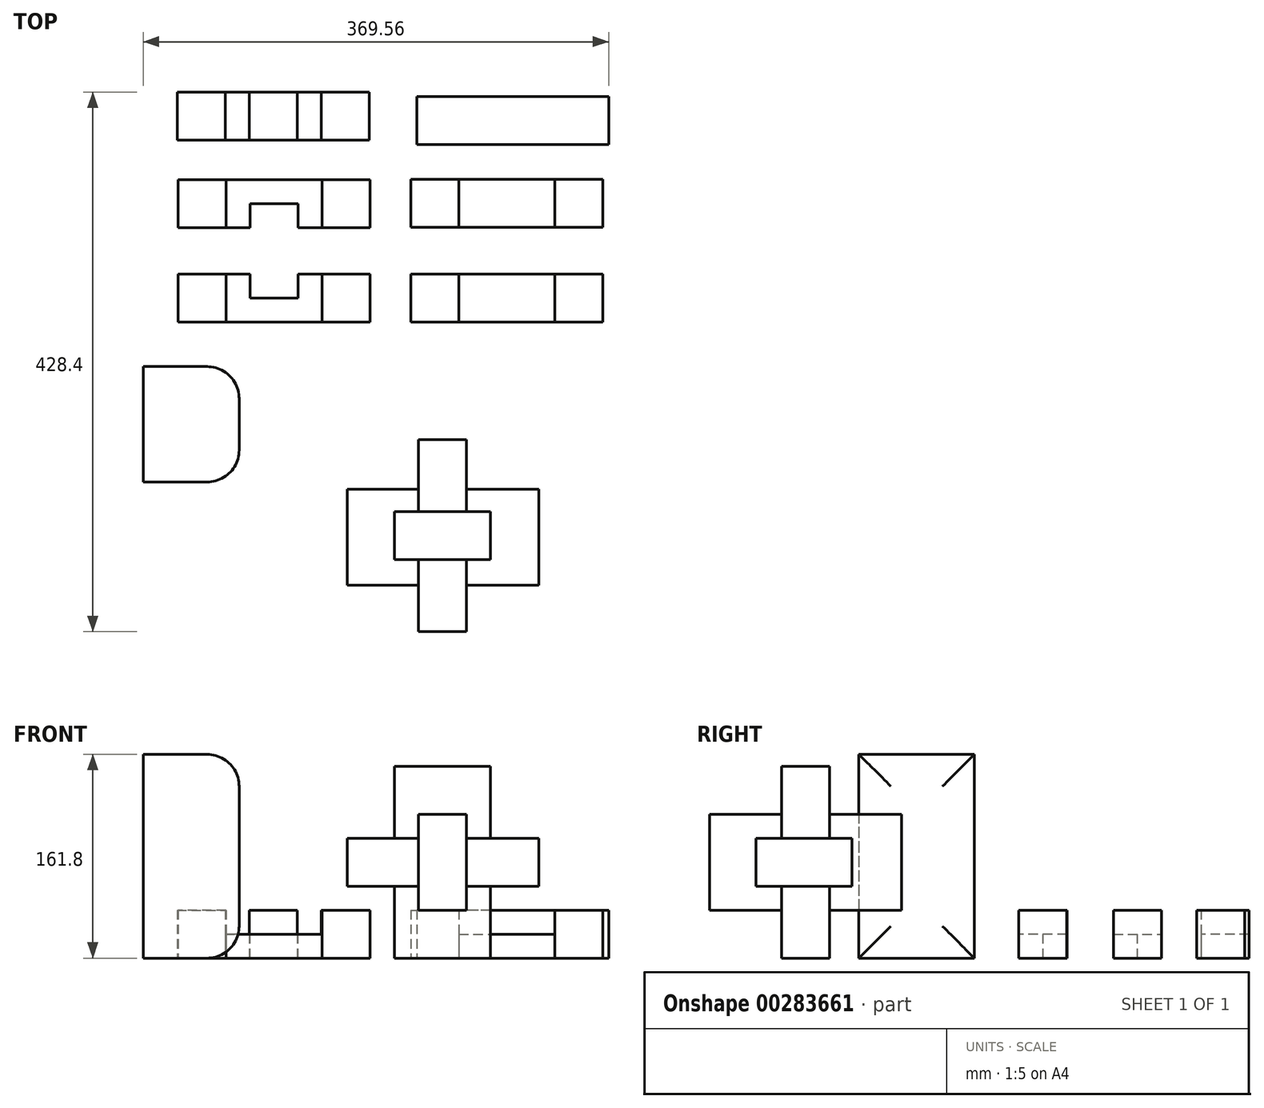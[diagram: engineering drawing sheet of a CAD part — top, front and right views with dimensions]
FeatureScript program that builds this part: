
annotation { "Feature Type Name" : "Feature", "Feature Type Description" : "" }
export const myFeature = defineFeature(function(context is Context, id is Id, definition is map)
    precondition{}
    {
        {
            var Q0;
            Q0=qCreatedBy(makeId("Top.planeOp"),FACE);
            var sketch = newSketch(context, id + "F0", { "sketchPlane" : qUnion([Q0])});
            skLineSegment(sketch, "E0", {"start": v(-72.38, -56.7) * mm, "end": v(80.02, -56.7) * mm});
            skLineSegment(sketch, "E1.top", {"start": v(-72.38, -18.6) * mm, "end": v(80.02, -18.6) * mm});
            skLineSegment(sketch, "E1.left", {"start": v(-72.38, -56.7) * mm, "end": v(-72.38, -18.6) * mm});
            skLineSegment(sketch, "E1.right", {"start": v(80.02, -56.7) * mm, "end": v(80.02, -18.6) * mm});
            skLineSegment(sketch, "E2", {"start": v(-72.38, -18.6) * mm, "end": v(-34.28, -18.6) * mm, "construction": true});
            skLineSegment(sketch, "E3", {"start": v(-34.28, -18.6) * mm, "end": v(3.82, -18.6) * mm, "construction": true});
            skLineSegment(sketch, "E4", {"start": v(3.82, -18.6) * mm, "end": v(41.92, -18.6) * mm, "construction": true});
            skLineSegment(sketch, "E5", {"start": v(41.92, -18.6) * mm, "end": v(80.02, -18.6) * mm, "construction": true});
            skLineSegment(sketch, "E6", {"start": v(-34.28, -18.6) * mm, "end": v(-34.28, -56.7) * mm});
            skLineSegment(sketch, "E7", {"start": v(41.92, -18.6) * mm, "end": v(41.92, -56.7) * mm});
            skSolve(sketch);
        }
        {
            var Q0;
            {var subQ0=sQuery(id+"F0.wireOp",EDGE,"E1.left");Q0=makeQuery(id+"F0.imprint","IMPRINT",FACE,{"disambiguationData":[TD([[makeQuery(id+"F0.imprint","IMPRINT",EDGE,{"derivedFrom":subQ0}),-1.0]])]});}
            var Q1;
            {var subQ0=sQuery(id+"F0.wireOp",EDGE,"E1.right");Q1=makeQuery(id+"F0.imprint","IMPRINT",FACE,{"disambiguationData":[TD([[makeQuery(id+"F0.imprint","IMPRINT",EDGE,{"derivedFrom":subQ0}),1.0]])]});}
            extrude(context, id + "F1", {"entities" : qUnion([Q0, Q1]), "depth" : 38.1 * mm});
        }
        {
            var Q0;
            {var subQ0=sQuery(id+"F0.wireOp",EDGE,"E6");Q0=makeQuery(id+"F0.imprint","IMPRINT",FACE,{"disambiguationData":[TD([[makeQuery(id+"F0.imprint","IMPRINT",EDGE,{"derivedFrom":subQ0}),1.0]])]});}
            extrude(context, id + "F2", {"entities" : qUnion([Q0]), "depth" : 19.05 * mm});
        }
        {
            var Q0;
            Q0=makeQuery(id+"F1.opExtrude","SWEPT_BODY",BODY,{"disambiguationData":[OSD([sQuery(id+"F0.wireOp",EDGE,"E0"),sQuery(id+"F0.wireOp",EDGE,"E1.top"),sQuery(id+"F0.wireOp",EDGE,"E1.left"),sQuery(id+"F0.wireOp",EDGE,"E6")])]});
            var Q1;
            Q1=makeQuery(id+"F2.opExtrude","SWEPT_BODY",BODY,{"disambiguationData":[OSD([sQuery(id+"F0.wireOp",EDGE,"E0"),sQuery(id+"F0.wireOp",EDGE,"E1.top"),sQuery(id+"F0.wireOp",EDGE,"E6"),sQuery(id+"F0.wireOp",EDGE,"E7")])]});
            var Q2;
            Q2=makeQuery(id+"F1.opExtrude","SWEPT_BODY",BODY,{"disambiguationData":[OSD([sQuery(id+"F0.wireOp",EDGE,"E0"),sQuery(id+"F0.wireOp",EDGE,"E1.top"),sQuery(id+"F0.wireOp",EDGE,"E1.right"),sQuery(id+"F0.wireOp",EDGE,"E7")])]});
            var Q3;
            Q3=qCreatedBy(makeId("Front.planeOp"),FACE);
            mirror(context, id + "F3", {"entities" : qUnion([Q0, Q1, Q2]), "mirrorPlane" : qUnion([Q3])});
        }
        {
            var Q0;
            Q0=qCreatedBy(makeId("Top.planeOp"),FACE);
            var sketch = newSketch(context, id + "F4", { "sketchPlane" : qUnion([Q0])});
            skLineSegment(sketch, "E8.bottom", {"start": v(-104.95, -56.55) * mm, "end": v(-257.35, -56.55) * mm});
            skLineSegment(sketch, "E8.top", {"start": v(-104.95, -18.45) * mm, "end": v(-257.35, -18.45) * mm});
            skLineSegment(sketch, "E8.left", {"start": v(-104.95, -56.55) * mm, "end": v(-104.95, -18.45) * mm});
            skLineSegment(sketch, "E8.right", {"start": v(-257.35, -56.55) * mm, "end": v(-257.35, -18.45) * mm});
            skLineSegment(sketch, "E9", {"start": v(-104.95, -18.45) * mm, "end": v(-143.05, -18.45) * mm, "construction": true});
            skLineSegment(sketch, "E10", {"start": v(-143.05, -18.45) * mm, "end": v(-257.35, -18.45) * mm, "construction": true});
            skLineSegment(sketch, "E11", {"start": v(-219.25, -18.45) * mm, "end": v(-257.35, -18.45) * mm, "construction": true});
            skLineSegment(sketch, "E12", {"start": v(-143.05, -18.45) * mm, "end": v(-143.05, -56.55) * mm});
            skLineSegment(sketch, "E13", {"start": v(-219.25, -18.45) * mm, "end": v(-219.25, -56.55) * mm});
            skSolve(sketch);
        }
        {
            var Q0;
            {var subQ0=sQuery(id+"F4.wireOp",EDGE,"E8.left");Q0=makeQuery(id+"F4.imprint","IMPRINT",FACE,{"disambiguationData":[TD([[makeQuery(id+"F4.imprint","IMPRINT",EDGE,{"derivedFrom":subQ0}),1.0]])]});}
            var Q1;
            {var subQ0=sQuery(id+"F4.wireOp",EDGE,"E8.right");Q1=makeQuery(id+"F4.imprint","IMPRINT",FACE,{"disambiguationData":[TD([[makeQuery(id+"F4.imprint","IMPRINT",EDGE,{"derivedFrom":subQ0}),-1.0]])]});}
            extrude(context, id + "F5", {"entities" : qUnion([Q0, Q1]), "operationType" : NewBodyOperationType.ADD, "depth" : 38.1 * mm});
        }
        {
            var Q0;
            {var subQ0=sQuery(id+"F4.wireOp",EDGE,"E12");Q0=makeQuery(id+"F4.imprint","IMPRINT",FACE,{"disambiguationData":[TD([[makeQuery(id+"F4.imprint","IMPRINT",EDGE,{"derivedFrom":subQ0}),-1.0]])]});}
            extrude(context, id + "F6", {"entities" : qUnion([Q0]), "depth" : 19.05 * mm});
        }
        {
            var Q0;
            Q0=makeQuery(id+"F6.opExtrude","CAP_FACE",FACE,{"disambiguationData":[OSD([sQuery(id+"F4.wireOp",EDGE,"E8.bottom"),sQuery(id+"F4.wireOp",EDGE,"E8.top"),sQuery(id+"F4.wireOp",EDGE,"E12"),sQuery(id+"F4.wireOp",EDGE,"E13")])],"isStart":false});
            var sketch = newSketch(context, id + "F7", { "sketchPlane" : qUnion([Q0])});
            skLineSegment(sketch, "E14", {"start": v(-219.25, -18.45) * mm, "end": v(-200.2, -18.45) * mm, "construction": true});
            skLineSegment(sketch, "E15", {"start": v(-200.2, -18.45) * mm, "end": v(-200.2, -37.5) * mm, "construction": true});
            skLineSegment(sketch, "E16", {"start": v(-200.2, -18.45) * mm, "end": v(-200.2, -37.5) * mm});
            skLineSegment(sketch, "E17", {"start": v(-162.1, -37.5) * mm, "end": v(-200.2, -37.5) * mm});
            skLineSegment(sketch, "E18", {"start": v(-162.1, -37.5) * mm, "end": v(-162.1, -18.45) * mm});
            skSolve(sketch);
        }
        {
            var Q0;
            {var subQ0=sQuery(id+"F7.wireOp",EDGE,"E16");Q0=makeQuery(id+"F7.imprint","IMPRINT",FACE,{"disambiguationData":[TD([[makeQuery(id+"F7.imprint","IMPRINT",EDGE,{"derivedFrom":subQ0}),1.0]])]});}
            extrude(context, id + "F8", {"entities" : qUnion([Q0]), "operationType" : NewBodyOperationType.REMOVE, "oppositeDirection" : true, "depth" : 19.05 * mm});
        }
        {
            var Q0;
            Q0=makeQuery(id+"F5.opExtrude","SWEPT_BODY",BODY,{"disambiguationData":[OSD([sQuery(id+"F4.wireOp",EDGE,"E8.bottom"),sQuery(id+"F4.wireOp",EDGE,"E8.top"),sQuery(id+"F4.wireOp",EDGE,"E8.left"),sQuery(id+"F4.wireOp",EDGE,"E12")])]});
            var Q1;
            Q1=makeQuery(id+"F6.opExtrude","SWEPT_BODY",BODY,{"disambiguationData":[OSD([sQuery(id+"F4.wireOp",EDGE,"E8.bottom"),sQuery(id+"F4.wireOp",EDGE,"E8.top"),sQuery(id+"F4.wireOp",EDGE,"E12"),sQuery(id+"F4.wireOp",EDGE,"E13")])]});
            var Q2;
            Q2=makeQuery(id+"F5.opExtrude","SWEPT_BODY",BODY,{"disambiguationData":[OSD([sQuery(id+"F4.wireOp",EDGE,"E8.bottom"),sQuery(id+"F4.wireOp",EDGE,"E8.top"),sQuery(id+"F4.wireOp",EDGE,"E8.right"),sQuery(id+"F4.wireOp",EDGE,"E13")])]});
            var Q3;
            Q3=qCreatedBy(makeId("Front.planeOp"),FACE);
            mirror(context, id + "F9", {"entities" : qUnion([Q0, Q1, Q2]), "mirrorPlane" : qUnion([Q3])});
        }
        {
            var Q0;
            Q0=qCreatedBy(makeId("Top.planeOp"),FACE);
            var sketch = newSketch(context, id + "F10", { "sketchPlane" : qUnion([Q0])});
            skLineSegment(sketch, "E19.bottom", {"start": v(84.58, 84.4) * mm, "end": v(-67.82, 84.4) * mm});
            skLineSegment(sketch, "E19.top", {"start": v(84.58, 122.5) * mm, "end": v(-67.82, 122.5) * mm});
            skLineSegment(sketch, "E19.left", {"start": v(84.58, 84.4) * mm, "end": v(84.58, 122.5) * mm});
            skLineSegment(sketch, "E19.right", {"start": v(-67.82, 84.4) * mm, "end": v(-67.82, 122.5) * mm});
            skSolve(sketch);
        }
        {
            var Q0;
            Q0=makeQuery(id+"F10.imprint","IMPRINT",FACE,{"disambiguationData":[TD([[makeQuery(id+"F10.imprint","IMPRINT",EDGE,{"derivedFrom":sQuery(id+"F10.wireOp",EDGE,"E19.bottom")}),-1.0]])]});
            extrude(context, id + "F11", {"entities" : qUnion([Q0]), "depth" : 38.1 * mm});
        }
        {
            var Q0;
            Q0=qCreatedBy(makeId("Top.planeOp"),FACE);
            var sketch = newSketch(context, id + "F12", { "sketchPlane" : qUnion([Q0])});
            skLineSegment(sketch, "E20.bottom", {"start": v(-257.97, 87.96) * mm, "end": v(-105.57, 87.96) * mm});
            skLineSegment(sketch, "E20.top", {"start": v(-257.97, 126.06) * mm, "end": v(-105.57, 126.06) * mm});
            skLineSegment(sketch, "E20.left", {"start": v(-257.97, 87.96) * mm, "end": v(-257.97, 126.06) * mm});
            skLineSegment(sketch, "E20.right", {"start": v(-105.57, 87.96) * mm, "end": v(-105.57, 126.06) * mm});
            skLineSegment(sketch, "E21.bottom", {"start": v(-257.97, 126.06) * mm, "end": v(-219.87, 126.06) * mm, "construction": true});
            skLineSegment(sketch, "E21.top", {"start": v(-257.97, 126.06) * mm, "end": v(-219.87, 126.06) * mm, "construction": true});
            skLineSegment(sketch, "E21.left", {"start": v(-257.97, 126.06) * mm, "end": v(-257.97, 126.06) * mm});
            skLineSegment(sketch, "E21.right", {"start": v(-219.87, 126.06) * mm, "end": v(-219.87, 126.06) * mm});
            skLineSegment(sketch, "E22.bottom", {"start": v(-105.57, 126.06) * mm, "end": v(-143.67, 126.06) * mm, "construction": true});
            skLineSegment(sketch, "E22.top", {"start": v(-105.57, 126.06) * mm, "end": v(-143.67, 126.06) * mm, "construction": true});
            skLineSegment(sketch, "E22.left", {"start": v(-105.57, 126.06) * mm, "end": v(-105.57, 126.06) * mm});
            skLineSegment(sketch, "E22.right", {"start": v(-143.67, 126.06) * mm, "end": v(-143.67, 126.06) * mm});
            skLineSegment(sketch, "E23.bottom", {"start": v(-219.87, 126.06) * mm, "end": v(-200.82, 126.06) * mm, "construction": true});
            skLineSegment(sketch, "E23.top", {"start": v(-219.87, 126.06) * mm, "end": v(-200.82, 126.06) * mm, "construction": true});
            skLineSegment(sketch, "E23.right", {"start": v(-200.82, 126.06) * mm, "end": v(-200.82, 126.06) * mm});
            skLineSegment(sketch, "E24.bottom", {"start": v(-143.67, 126.06) * mm, "end": v(-162.72, 126.06) * mm, "construction": true});
            skLineSegment(sketch, "E24.top", {"start": v(-143.67, 126.06) * mm, "end": v(-162.72, 126.06) * mm, "construction": true});
            skLineSegment(sketch, "E24.right", {"start": v(-162.72, 126.06) * mm, "end": v(-162.72, 126.06) * mm});
            skLineSegment(sketch, "E25", {"start": v(-219.87, 126.06) * mm, "end": v(-219.87, 87.96) * mm});
            skLineSegment(sketch, "E26", {"start": v(-200.82, 126.06) * mm, "end": v(-200.82, 87.96) * mm});
            skLineSegment(sketch, "E27", {"start": v(-162.72, 126.06) * mm, "end": v(-162.72, 87.96) * mm});
            skLineSegment(sketch, "E28", {"start": v(-143.67, 126.06) * mm, "end": v(-143.67, 87.96) * mm});
            skSolve(sketch);
        }
        {
            var Q0;
            {var subQ0=sQuery(id+"F12.wireOp",EDGE,"E20.left");Q0=makeQuery(id+"F12.imprint","IMPRINT",FACE,{"disambiguationData":[TD([[makeQuery(id+"F12.imprint","IMPRINT",EDGE,{"derivedFrom":subQ0}),-1.0]])]});}
            var Q1;
            {var subQ0=sQuery(id+"F12.wireOp",EDGE,"E26");Q1=makeQuery(id+"F12.imprint","IMPRINT",FACE,{"disambiguationData":[TD([[makeQuery(id+"F12.imprint","IMPRINT",EDGE,{"derivedFrom":subQ0}),1.0]])]});}
            var Q2;
            {var subQ0=sQuery(id+"F12.wireOp",EDGE,"E20.right");Q2=makeQuery(id+"F12.imprint","IMPRINT",FACE,{"disambiguationData":[TD([[makeQuery(id+"F12.imprint","IMPRINT",EDGE,{"derivedFrom":subQ0}),1.0]])]});}
            extrude(context, id + "F13", {"entities" : qUnion([Q0, Q1, Q2]), "depth" : 38.1 * mm});
        }
        {
            var Q0;
            {var subQ0=sQuery(id+"F12.wireOp",EDGE,"E25");Q0=makeQuery(id+"F12.imprint","IMPRINT",FACE,{"disambiguationData":[TD([[makeQuery(id+"F12.imprint","IMPRINT",EDGE,{"derivedFrom":subQ0}),1.0]])]});}
            var Q1;
            {var subQ0=sQuery(id+"F12.wireOp",EDGE,"E27");Q1=makeQuery(id+"F12.imprint","IMPRINT",FACE,{"disambiguationData":[TD([[makeQuery(id+"F12.imprint","IMPRINT",EDGE,{"derivedFrom":subQ0}),1.0]])]});}
            extrude(context, id + "F14", {"entities" : qUnion([Q0, Q1]), "depth" : 19.05 * mm});
        }
        {
            var Q0;
            Q0=qCreatedBy(makeId("Top.planeOp"),FACE);
            var sketch = newSketch(context, id + "F15", { "sketchPlane" : qUnion([Q0])});
            skLineSegment(sketch, "E29.bottom", {"start": v(-85.56, -207.1) * mm, "end": v(-9.36, -207.1) * mm});
            skLineSegment(sketch, "E29.top", {"start": v(-85.56, -245.2) * mm, "end": v(-9.36, -245.2) * mm});
            skLineSegment(sketch, "E29.left", {"start": v(-85.56, -207.1) * mm, "end": v(-85.56, -245.2) * mm});
            skLineSegment(sketch, "E29.right", {"start": v(-9.36, -207.1) * mm, "end": v(-9.36, -245.2) * mm});
            skSolve(sketch);
        }
        {
            var Q0;
            Q0=makeQuery(id+"F15.imprint","IMPRINT",FACE,{"disambiguationData":[TD([[makeQuery(id+"F15.imprint","IMPRINT",EDGE,{"derivedFrom":sQuery(id+"F15.wireOp",EDGE,"E29.bottom")}),-1.0]])]});
            extrude(context, id + "F16", {"entities" : qUnion([Q0]), "depth" : 152.4 * mm});
        }
        {
            var Q0;
            Q0=qCreatedBy(makeId("Right.planeOp"),FACE);
            var sketch = newSketch(context, id + "F17", { "sketchPlane" : qUnion([Q0])});
            skLineSegment(sketch, "E30", {"start": v(-208.36, 152.4) * mm, "end": v(-208.36, 0) * mm, "construction": true});
            skLineSegment(sketch, "E31", {"start": v(-208.36, 0) * mm, "end": v(-208.36, 76.2) * mm, "construction": true});
            skLineSegment(sketch, "E32", {"start": v(-208.36, 76.2) * mm, "end": v(-208.36, 38.1) * mm, "construction": true});
            skLineSegment(sketch, "E33", {"start": v(-208.36, 76.2) * mm, "end": v(-208.36, 57.15) * mm, "construction": true});
            skLineSegment(sketch, "E34", {"start": v(-208.36, 57.15) * mm, "end": v(-208.36, 95.25) * mm, "construction": true});
            skLineSegment(sketch, "E35", {"start": v(-208.36, 76.2) * mm, "end": v(-189.3, 76.2) * mm, "construction": true});
            skLineSegment(sketch, "E36", {"start": v(-189.3, 76.2) * mm, "end": v(-189.3, 57.15) * mm, "construction": true});
            skLineSegment(sketch, "E37", {"start": v(-189.3, 57.15) * mm, "end": v(-265.5, 57.15) * mm});
            skLineSegment(sketch, "E38", {"start": v(-265.5, 57.15) * mm, "end": v(-265.5, 95.25) * mm});
            skLineSegment(sketch, "E39", {"start": v(-265.5, 95.25) * mm, "end": v(-189.3, 95.25) * mm});
            skLineSegment(sketch, "E40", {"start": v(-189.3, 95.25) * mm, "end": v(-189.3, 57.15) * mm});
            skSolve(sketch);
        }
        {
            var Q0;
            Q0=makeQuery(id+"F16.opExtrude","SWEPT_FACE",FACE,{"disambiguationData":[OSD([sQuery(id+"F15.wireOp",EDGE,"E29.top")])]});
            var sketch = newSketch(context, id + "F18", { "sketchPlane" : qUnion([Q0])});
            skLineSegment(sketch, "E41", {"start": v(-47.46, 152.4) * mm, "end": v(-47.46, 114.3) * mm, "construction": true});
            skLineSegment(sketch, "E42", {"start": v(-47.46, 0) * mm, "end": v(-47.46, 38.1) * mm, "construction": true});
            skLineSegment(sketch, "E43", {"start": v(-85.56, 76.2) * mm, "end": v(-66.5, 76.2) * mm, "construction": true});
            skLineSegment(sketch, "E44.bottom", {"start": v(-66.5, 114.3) * mm, "end": v(-28.4, 114.3) * mm});
            skLineSegment(sketch, "E44.top", {"start": v(-66.5, 38.1) * mm, "end": v(-28.4, 38.1) * mm});
            skLineSegment(sketch, "E44.left", {"start": v(-66.5, 114.3) * mm, "end": v(-66.5, 38.1) * mm});
            skLineSegment(sketch, "E44.right", {"start": v(-28.4, 114.3) * mm, "end": v(-28.4, 38.1) * mm});
            skSolve(sketch);
        }
        {
            var Q0;
            Q0=makeQuery(id+"F18.imprint","IMPRINT",FACE,{"disambiguationData":[TD([[makeQuery(id+"F18.imprint","IMPRINT",EDGE,{"derivedFrom":sQuery(id+"F18.wireOp",EDGE,"E44.bottom")}),-1.0]])]});
            extrude(context, id + "F19", {"entities" : qUnion([Q0]), "operationType" : NewBodyOperationType.ADD, "depth" : 57.15 * mm});
        }
        {
            var Q0;
            Q0=makeQuery(id+"F16.opExtrude","SWEPT_FACE",FACE,{"disambiguationData":[OSD([sQuery(id+"F15.wireOp",EDGE,"E29.bottom")])]});
            var sketch = newSketch(context, id + "F20", { "sketchPlane" : qUnion([Q0])});
            skLineSegment(sketch, "E45", {"start": v(47.46, 152.4) * mm, "end": v(47.46, 114.3) * mm, "construction": true});
            skLineSegment(sketch, "E46", {"start": v(9.36, 76.2) * mm, "end": v(28.4, 76.2) * mm, "construction": true});
            skLineSegment(sketch, "E47.bottom", {"start": v(28.4, 114.3) * mm, "end": v(66.5, 114.3) * mm});
            skLineSegment(sketch, "E47.top", {"start": v(28.4, 38.1) * mm, "end": v(66.5, 38.1) * mm});
            skLineSegment(sketch, "E47.left", {"start": v(28.4, 114.3) * mm, "end": v(28.4, 38.1) * mm});
            skLineSegment(sketch, "E47.right", {"start": v(66.5, 114.3) * mm, "end": v(66.5, 38.1) * mm});
            skSolve(sketch);
        }
        {
            var Q0;
            Q0=makeQuery(id+"F20.imprint","IMPRINT",FACE,{"disambiguationData":[TD([[makeQuery(id+"F20.imprint","IMPRINT",EDGE,{"derivedFrom":sQuery(id+"F20.wireOp",EDGE,"E47.bottom")}),-1.0]])]});
            extrude(context, id + "F21", {"entities" : qUnion([Q0]), "operationType" : NewBodyOperationType.ADD, "depth" : 57.15 * mm});
        }
        {
            var Q0;
            Q0=makeQuery(id+"F16.opExtrude","SWEPT_FACE",FACE,{"disambiguationData":[OSD([sQuery(id+"F15.wireOp",EDGE,"E29.top")])]});
            var sketch = newSketch(context, id + "F22", { "sketchPlane" : qUnion([Q0])});
            skLineSegment(sketch, "E48", {"start": v(-85.56, 76.2) * mm, "end": v(-123.66, 76.2) * mm, "construction": true});
            skSolve(sketch);
        }
        {
            var Q0;
            Q0=makeQuery(id+"F17.imprint","IMPRINT",FACE,{"disambiguationData":[TD([[makeQuery(id+"F17.imprint","IMPRINT",EDGE,{"derivedFrom":sQuery(id+"F17.wireOp",EDGE,"E37")}),-1.0]])]});
            extrude(context, id + "F23", {"entities" : qUnion([Q0]), "operationType" : NewBodyOperationType.ADD, "oppositeDirection" : true, "depth" : 122.94 * mm});
        }
        {
            var Q0;
            Q0=makeQuery(id+"F23.opExtrude","CAP_FACE",FACE,{"disambiguationData":[OSD([sQuery(id+"F17.wireOp",EDGE,"E37"),sQuery(id+"F17.wireOp",EDGE,"E38"),sQuery(id+"F17.wireOp",EDGE,"E39"),sQuery(id+"F17.wireOp",EDGE,"E40")])],"isStart":true});
            extrude(context, id + "F24", {"entities" : qUnion([Q0]), "operationType" : NewBodyOperationType.ADD, "depth" : 29.2 * mm});
        }
        {
            var Q0;
            Q0=qCreatedBy(makeId("Top.planeOp"),FACE);
            var sketch = newSketch(context, id + "F25", { "sketchPlane" : qUnion([Q0])});
            skLineSegment(sketch, "E49.bottom", {"start": v(-284.98, -92) * mm, "end": v(-208.78, -92) * mm});
            skLineSegment(sketch, "E49.top", {"start": v(-284.98, -183.65) * mm, "end": v(-208.78, -183.65) * mm});
            skLineSegment(sketch, "E49.left", {"start": v(-284.98, -92) * mm, "end": v(-284.98, -183.65) * mm});
            skLineSegment(sketch, "E49.right", {"start": v(-208.78, -92) * mm, "end": v(-208.78, -183.65) * mm});
            skSolve(sketch);
        }
        {
            var Q0;
            Q0=makeQuery(id+"F25.imprint","IMPRINT",FACE,{"disambiguationData":[TD([[makeQuery(id+"F25.imprint","IMPRINT",EDGE,{"derivedFrom":sQuery(id+"F25.wireOp",EDGE,"E49.bottom")}),-1.0]])]});
            extrude(context, id + "F26", {"entities" : qUnion([Q0]), "depth" : 161.8 * mm});
        }
        {
            var Q0;
            Q0=makeQuery(id+"F26.opExtrude","SWEPT_FACE",FACE,{"disambiguationData":[OSD([sQuery(id+"F25.wireOp",EDGE,"E49.right")])]});
            fillet(context, id + "F27", {"entities" : qUnion([Q0]), "radius" : 25.4 * mm, "tangentPropagation" : true, "allowEdgeOverflow" : false});
        }
    });
